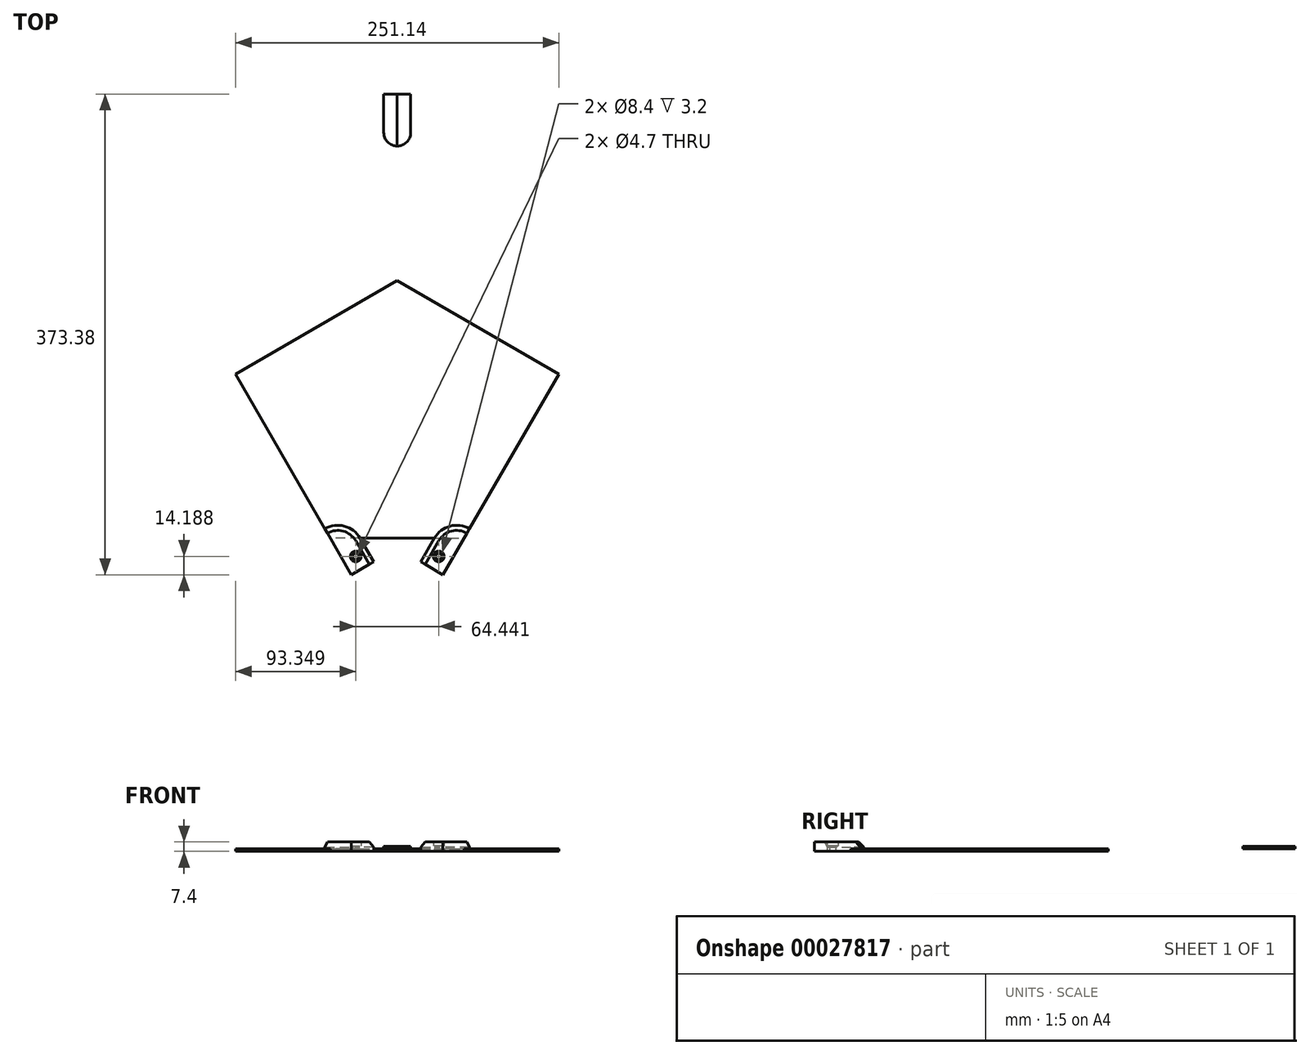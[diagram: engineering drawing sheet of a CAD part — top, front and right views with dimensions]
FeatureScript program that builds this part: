
annotation { "Feature Type Name" : "Feature", "Feature Type Description" : "" }
export const myFeature = defineFeature(function(context is Context, id is Id, definition is map)
    precondition{}
    {
        {
            var Q0;
            Q0=qCreatedBy(makeId("Top.planeOp"),FACE);
            var sketch = newSketch(context, id + "F0", { "sketchPlane" : qUnion([Q0])});
            skCircle(sketch, "E0.cCircle", {"center": v(0, 0) * mm, "radius": 145 * mm, "construction": true});
            skLineSegment(sketch, "E0.0", {"start": v(251.15, 145) * mm, "end": v(0, -290) * mm});
            skLineSegment(sketch, "E0.1", {"start": v(0, -290) * mm, "end": v(-251.15, 145) * mm});
            skLineSegment(sketch, "E0.2", {"start": v(-251.15, 145) * mm, "end": v(251.15, 145) * mm});
            skPoint(sketch, "E0.0.midPoint", {"position": v(125.57, -72.5) * mm});
            skLineSegment(sketch, "E1.bottom", {"start": v(-180, 145) * mm, "end": v(180, 145) * mm});
            skLineSegment(sketch, "E1.top", {"start": v(-180, 125) * mm, "end": v(180, 125) * mm});
            skLineSegment(sketch, "E1.left", {"start": v(-180, 125) * mm, "end": v(-180, 145) * mm});
            skLineSegment(sketch, "E1.right", {"start": v(180, 125) * mm, "end": v(180, 145) * mm});
            skLineSegment(sketch, "E2", {"start": v(0, -200) * mm, "end": v(0, 125) * mm, "construction": true});
            skPoint(sketch, "E3", {"position": v(0, 145) * mm});
            skCircle(sketch, "E4", {"center": v(0, 0) * mm, "radius": 118.5 * mm, "construction": true});
            skLineSegment(sketch, "E5", {"start": v(-51.96, -200) * mm, "end": v(51.96, -200) * mm});
            skLineSegment(sketch, "E6", {"start": v(0, 0) * mm, "end": v(-125.57, -72.5) * mm});
            skLineSegment(sketch, "E7", {"start": v(0, 0) * mm, "end": v(125.57, -72.5) * mm});
            skLineSegment(sketch, "E8.1.0", {"start": v(-18.25, -218.38) * mm, "end": v(-198.25, 93.38) * mm});
            skLineSegment(sketch, "E8.1.1", {"start": v(-18.25, -218.38) * mm, "end": v(-35.57, -228.38) * mm});
            skLineSegment(sketch, "E8.1.2", {"start": v(-35.57, -228.38) * mm, "end": v(-215.57, 83.38) * mm});
            skLineSegment(sketch, "E8.1.3", {"start": v(-198.25, 93.38) * mm, "end": v(-215.57, 83.38) * mm});
            skPoint(sketch, "E8.1.4", {"position": v(-125.57, -72.5) * mm});
            skPoint(sketch, "E8.1.5", {"position": v(-125.57, -72.5) * mm});
            skLineSegment(sketch, "E8.2.0", {"start": v(198.25, 93.38) * mm, "end": v(28.87, -200) * mm});
            skLineSegment(sketch, "E8.2.1", {"start": v(198.25, 93.38) * mm, "end": v(215.57, 83.38) * mm});
            skLineSegment(sketch, "E8.2.2", {"start": v(215.57, 83.38) * mm, "end": v(35.57, -228.38) * mm});
            skLineSegment(sketch, "E8.2.3", {"start": v(18.25, -218.38) * mm, "end": v(35.57, -228.38) * mm});
            skLineSegment(sketch, "E9", {"start": v(51.96, -200) * mm, "end": v(34.64, -190) * mm, "construction": true});
            skLineSegment(sketch, "E10", {"start": v(28.87, -200) * mm, "end": v(18.25, -218.38) * mm});
            skArc(sketch, "E11", {"start": v(56.19, -192.68) * mm, "mid": v(41.01, -190.68) * mm, "end": v(28.87, -200) * mm});
            skLineSegment(sketch, "E12", {"start": v(18.25, -218.38) * mm, "end": v(46.19, -210) * mm, "construction": true});
            skLineSegment(sketch, "E13", {"start": v(35.57, -228.38) * mm, "end": v(28.87, -200) * mm, "construction": true});
            skLineSegment(sketch, "E14", {"start": v(46.19, -210) * mm, "end": v(28.87, -200) * mm, "construction": true});
            skCircle(sketch, "E15", {"center": v(32.22, -214.2) * mm, "radius": 2.35 * mm});
            skCircle(sketch, "E16", {"center": v(32.22, -214.2) * mm, "radius": 4.2 * mm});
            skSolve(sketch);
        }
        {
            var Q0;
            {var subQ0=sQuery(id+"F0.wireOp",EDGE,"E8.2.3");Q0=makeQuery(id+"F0.imprint","IMPRINT",FACE,{"disambiguationData":[TD([[makeQuery(id+"F0.imprint","IMPRINT",EDGE,{"derivedFrom":subQ0}),1.0]])]});}
            var Q1;
            {var subQ0=sQuery(id+"F0.wireOp",EDGE,"E11");Q1=makeQuery(id+"F0.imprint","IMPRINT",FACE,{"disambiguationData":[TD([[makeQuery(id+"F0.imprint","IMPRINT",EDGE,{"derivedFrom":subQ0}),1.0]])]});}
            extrude(context, id + "F1", {"entities" : qUnion([Q0, Q1]), "depth" : 7.4 * mm});
        }
        {
            var Q0;
            Q0=makeQuery(id+"F0.imprint","IMPRINT",FACE,{"disambiguationData":[TD([[makeQuery(id+"F0.imprint","IMPRINT",EDGE,{"derivedFrom":sQuery(id+"F0.wireOp",EDGE,"E15")}),-1.0]])]});
            extrude(context, id + "F2", {"entities" : qUnion([Q0]), "operationType" : NewBodyOperationType.ADD, "depth" : 4.2 * mm});
        }
        {
            var Q0;
            {var subQ0=sQuery(id+"F0.wireOp",EDGE,"E11");Q0=makeQuery(id+"F0.imprint","IMPRINT",FACE,{"disambiguationData":[TD([[makeQuery(id+"F0.imprint","IMPRINT",EDGE,{"derivedFrom":subQ0}),1.0]])]});}
            extrude(context, id + "F3", {"entities" : qUnion([Q0]), "operationType" : NewBodyOperationType.REMOVE, "depth" : 2 * mm});
        }
        {
            var Q0;
            Q0=makeQuery(id+"F1.opExtrude","CAP_EDGE",EDGE,{"disambiguationData":[OSD([sQuery(id+"F0.wireOp",EDGE,"E8.2.2")])],"isStart":false});
            var Q1;
            Q1=makeQuery(id+"F1.opExtrude","CAP_EDGE",EDGE,{"disambiguationData":[OSD([sQuery(id+"F0.wireOp",EDGE,"E11")])],"isStart":false});
            chamfer(context, id + "F4", {"entities" : qUnion([Q0, Q1]), "width" : 4 * mm, "tangentPropagation" : true});
        }
        {
            var Q0;
            Q0=makeQuery(id+"F1.opExtrude","SWEPT_BODY",BODY,{"disambiguationData":[OSD([sQuery(id+"F0.wireOp",EDGE,"E8.2.2"),sQuery(id+"F0.wireOp",EDGE,"E8.2.3"),sQuery(id+"F0.wireOp",EDGE,"E10"),sQuery(id+"F0.wireOp",EDGE,"E11"),sQuery(id+"F0.wireOp",EDGE,"E16")])]});
            var Q1;
            Q1=qCreatedBy(makeId("Right.planeOp"),FACE);
            mirror(context, id + "F5", {"entities" : qUnion([Q0]), "mirrorPlane" : qUnion([Q1])});
        }
        {
            var Q0;
            {var subQ0=sQuery(id+"F0.wireOp",EDGE,"E8.1.2");var subQ3=sQuery(id+"F0.wireOp",EDGE,"E5");var subQ4=makeQuery(id+"F0.imprint","INTERSECT",VERTEX,{"derivedFrom":[subQ3,subQ0]});Q0=makeQuery(id+"F0.imprint","IMPRINT",FACE,{"disambiguationData":[TD([[makeQuery(id+"F0.imprint","IMPRINT",EDGE,{"disambiguationData":[TD([[subQ4,-1.0]])],"derivedFrom":subQ3}),1.0]])]});}
            var Q1;
            {var subQ1=sQuery(id+"F0.wireOp",EDGE,"E7");var subQ5=sQuery(id+"F0.wireOp",EDGE,"E6");var subQ6=makeQuery(id+"F0.imprint","INTERSECT",VERTEX,{"derivedFrom":[subQ5,subQ1]});Q1=makeQuery(id+"F0.imprint","IMPRINT",FACE,{"disambiguationData":[TD([[makeQuery(id+"F0.imprint","IMPRINT",EDGE,{"disambiguationData":[TD([[subQ6,-1.0]])],"derivedFrom":subQ5}),1.0]])]});}
            var Q2;
            {var subQ0=sQuery(id+"F0.wireOp",EDGE,"E11");Q2=makeQuery(id+"F0.imprint","IMPRINT",FACE,{"disambiguationData":[TD([[makeQuery(id+"F0.imprint","IMPRINT",EDGE,{"derivedFrom":subQ0}),-1.0]])]});}
            var Q3;
            {var subQ0=sQuery(id+"F0.wireOp",EDGE,"E11");Q3=makeQuery(id+"F0.imprint","IMPRINT",FACE,{"disambiguationData":[TD([[makeQuery(id+"F0.imprint","IMPRINT",EDGE,{"derivedFrom":subQ0}),1.0]])]});}
            extrude(context, id + "F6", {"entities" : qUnion([Q0, Q1, Q2, Q3]), "depth" : 2 * mm});
        }
        {
            var Q0;
            Q0=makeQuery(id+"F6.opExtrude","CAP_FACE",FACE,{"disambiguationData":[OSD([sQuery(id+"F0.wireOp",EDGE,"E5"),sQuery(id+"F0.wireOp",EDGE,"E6"),sQuery(id+"F0.wireOp",EDGE,"E7"),sQuery(id+"F0.wireOp",EDGE,"E8.1.2"),sQuery(id+"F0.wireOp",EDGE,"E8.2.2")])],"isStart":false});
            var sketch = newSketch(context, id + "F7", { "sketchPlane" : qUnion([Q0])});
            skLineSegment(sketch, "E17.0", {"start": v(-10.5, 145) * mm, "end": v(10.5, 145) * mm});
            skLineSegment(sketch, "E18", {"start": v(-10.5, 145) * mm, "end": v(-10.5, 115) * mm});
            skLineSegment(sketch, "E19.MirrorCS", {"start": v(10.5, 145) * mm, "end": v(10.5, 115) * mm});
            skArc(sketch, "E20", {"start": v(-10.5, 115) * mm, "mid": v(0, 104.5) * mm, "end": v(10.5, 115) * mm});
            skPoint(sketch, "E21.orphan", {"position": v(251.15, 145) * mm});
            skPoint(sketch, "E22.orphan", {"position": v(-251.15, 145) * mm});
            skLineSegment(sketch, "E23", {"start": v(0, 145) * mm, "end": v(0, 104.5) * mm});
            skSolve(sketch);
        }
        {
            var Q0;
            {var subQ1=sQuery(id+"F7.wireOp",EDGE,"E18");Q0=makeQuery(id+"F7.imprint","IMPRINT",FACE,{"disambiguationData":[TD([[makeQuery(id+"F7.imprint","IMPRINT",EDGE,{"derivedFrom":subQ1}),1.0]])]});}
            extrude(context, id + "F8", {"entities" : qUnion([Q0]), "depth" : 2 * mm});
        }
        {
            var Q0;
            {var subQ2=sQuery(id+"F7.wireOp",EDGE,"E19.MirrorCS");Q0=makeQuery(id+"F7.imprint","IMPRINT",FACE,{"disambiguationData":[TD([[makeQuery(id+"F7.imprint","IMPRINT",EDGE,{"derivedFrom":subQ2}),-1.0]])]});}
            extrude(context, id + "F9", {"entities" : qUnion([Q0]), "depth" : 2 * mm});
        }
    });
